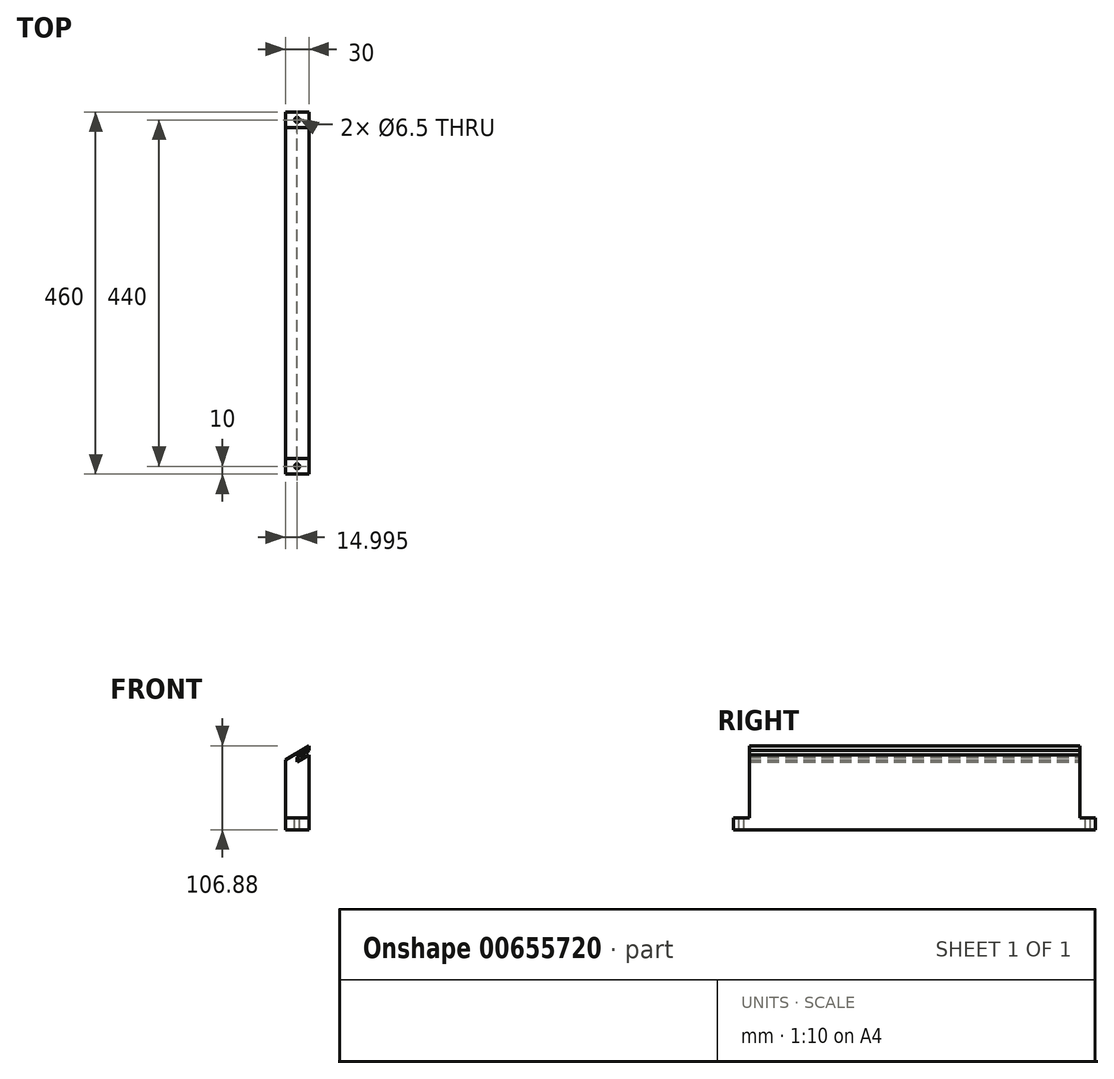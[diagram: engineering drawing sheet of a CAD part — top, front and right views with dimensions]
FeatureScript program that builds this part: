
annotation { "Feature Type Name" : "Feature", "Feature Type Description" : "" }
export const myFeature = defineFeature(function(context is Context, id is Id, definition is map)
    precondition{}
    {
        {
            var Q0;
            Q0=qCreatedBy(makeId("Front.planeOp"),FACE);
            var sketch = newSketch(context, id + "F0", { "sketchPlane" : qUnion([Q0])});
            skLineSegment(sketch, "E0", {"start": v(-11.31, 38.22) * mm, "end": v(18.69, 56.1) * mm});
            skLineSegment(sketch, "E1", {"start": v(-11.31, 38.22) * mm, "end": v(-11.31, -50.78) * mm});
            skLineSegment(sketch, "E2.trimOffspring", {"start": v(18.69, 38.64) * mm, "end": v(18.69, 44.46) * mm});
            skLineSegment(sketch, "E3.0", {"start": v(-11.31, -50.78) * mm, "end": v(18.69, -50.78) * mm});
            skLineSegment(sketch, "E4", {"start": v(18.69, -35.78) * mm, "end": v(18.69, -50.78) * mm});
            skLineSegment(sketch, "E5.0", {"start": v(3.69, 41.34) * mm, "end": v(18.69, 50.28) * mm});
            skLineSegment(sketch, "E6.0", {"start": v(3.69, 35.52) * mm, "end": v(16.13, 42.93) * mm});
            skLineSegment(sketch, "E7.0", {"start": v(3.69, 38.64) * mm, "end": v(3.69, 41.34) * mm});
            skLineSegment(sketch, "E8", {"start": v(3.69, 38.64) * mm, "end": v(3.69, 35.52) * mm});
            skLineSegment(sketch, "E9", {"start": v(16.13, 42.93) * mm, "end": v(18.69, 44.46) * mm});
            skLineSegment(sketch, "E10.trimOffspring", {"start": v(18.69, 50.28) * mm, "end": v(18.69, 56.1) * mm});
            skLineSegment(sketch, "E11", {"start": v(18.69, 38.64) * mm, "end": v(18.69, -35.78) * mm});
            skSolve(sketch);
        }
        {
            var Q0;
            Q0=makeQuery(id+"F0.imprint","IMPRINT",FACE,{"disambiguationData":[TD([[makeQuery(id+"F0.imprint","IMPRINT",EDGE,{"derivedFrom":sQuery(id+"F0.wireOp",EDGE,"E0")}),-1.0]])]});
            extrude(context, id + "F1", {"entities" : qUnion([Q0]), "depth" : 460 * mm, "offsetDistance" : 25 * mm});
        }
        {
            var Q0;
            Q0=makeQuery(id+"F1.opExtrude","CAP_FACE",FACE,{"disambiguationData":[OSD([sQuery(id+"F0.wireOp",EDGE,"E0"),sQuery(id+"F0.wireOp",EDGE,"E1"),sQuery(id+"F0.wireOp",EDGE,"E2.trimOffspring"),sQuery(id+"F0.wireOp",EDGE,"E3.0"),sQuery(id+"F0.wireOp",EDGE,"E4"),sQuery(id+"F0.wireOp",EDGE,"E5.0"),sQuery(id+"F0.wireOp",EDGE,"E6.0"),sQuery(id+"F0.wireOp",EDGE,"E7.0"),sQuery(id+"F0.wireOp",EDGE,"E8"),sQuery(id+"F0.wireOp",EDGE,"E9"),sQuery(id+"F0.wireOp",EDGE,"E10.trimOffspring"),sQuery(id+"F0.wireOp",EDGE,"E11")])],"isStart":false});
            var sketch = newSketch(context, id + "F2", { "sketchPlane" : qUnion([Q0])});
            skLineSegment(sketch, "E12.bottom", {"start": v(-11.31, -35.78) * mm, "end": v(18.69, -35.78) * mm});
            skLineSegment(sketch, "E12.top", {"start": v(-11.31, 57.22) * mm, "end": v(18.69, 57.22) * mm});
            skLineSegment(sketch, "E12.left", {"start": v(-11.31, -35.78) * mm, "end": v(-11.31, 57.22) * mm});
            skLineSegment(sketch, "E12.right", {"start": v(18.69, -35.78) * mm, "end": v(18.69, 57.22) * mm});
            skSolve(sketch);
        }
        {
            var Q0;
            Q0 = qSketchRegion(id + "F2", true);
            extrude(context, id + "F3", {"entities" : qUnion([Q0]), "operationType" : NewBodyOperationType.REMOVE, "oppositeDirection" : true, "depth" : 20 * mm, "offsetDistance" : 25 * mm});
        }
        {
            var Q0;
            Q0=makeQuery(id+"F1.opExtrude","CAP_FACE",FACE,{"disambiguationData":[OSD([sQuery(id+"F0.wireOp",EDGE,"E0"),sQuery(id+"F0.wireOp",EDGE,"E1"),sQuery(id+"F0.wireOp",EDGE,"E2.trimOffspring"),sQuery(id+"F0.wireOp",EDGE,"E3.0"),sQuery(id+"F0.wireOp",EDGE,"E4"),sQuery(id+"F0.wireOp",EDGE,"E5.0"),sQuery(id+"F0.wireOp",EDGE,"E6.0"),sQuery(id+"F0.wireOp",EDGE,"E7.0"),sQuery(id+"F0.wireOp",EDGE,"E8"),sQuery(id+"F0.wireOp",EDGE,"E9"),sQuery(id+"F0.wireOp",EDGE,"E10.trimOffspring"),sQuery(id+"F0.wireOp",EDGE,"E11")])],"isStart":true});
            var sketch = newSketch(context, id + "F4", { "sketchPlane" : qUnion([Q0])});
            skLineSegment(sketch, "E13.bottom", {"start": v(-18.69, -35.78) * mm, "end": v(11.31, -35.78) * mm});
            skLineSegment(sketch, "E13.left", {"start": v(-18.69, -35.78) * mm, "end": v(-18.69, 57.22) * mm});
            skLineSegment(sketch, "E13.right", {"start": v(11.31, -35.78) * mm, "end": v(11.31, -26.78) * mm});
            skLineSegment(sketch, "E14", {"start": v(-18.69, 57.22) * mm, "end": v(11.31, 57.22) * mm});
            skLineSegment(sketch, "E15", {"start": v(11.31, 57.22) * mm, "end": v(11.31, -26.78) * mm});
            skSolve(sketch);
        }
        {
            var Q0;
            Q0 = qSketchRegion(id + "F4", true);
            extrude(context, id + "F5", {"entities" : qUnion([Q0]), "operationType" : NewBodyOperationType.REMOVE, "oppositeDirection" : true, "depth" : 20 * mm, "offsetDistance" : 25 * mm});
        }
        {
            var Q0;
            Q0=makeQuery(id+"F5.boolean.opBoolean","COPY",FACE,{"derivedFrom":makeQuery(id+"F5.opExtrude","SWEPT_FACE",FACE,{"disambiguationData":[OSD([sQuery(id+"F4.wireOp",EDGE,"E13.bottom")])]})});
            var sketch = newSketch(context, id + "F6", { "sketchPlane" : qUnion([Q0])});
            skCircle(sketch, "E16", {"center": v(3.69, -10) * mm, "radius": 3.25 * mm});
            skCircle(sketch, "E17", {"center": v(3.69, -450) * mm, "radius": 3.25 * mm});
            skSolve(sketch);
        }
        {
            var Q0;
            Q0 = qSketchRegion(id + "F6", true);
            extrude(context, id + "F7", {"entities" : qUnion([Q0]), "operationType" : NewBodyOperationType.REMOVE, "endBound" : BoundingType.THROUGH_ALL, "oppositeDirection" : true, "depth" : 25 * mm, "offsetDistance" : 25 * mm});
        }
    });
